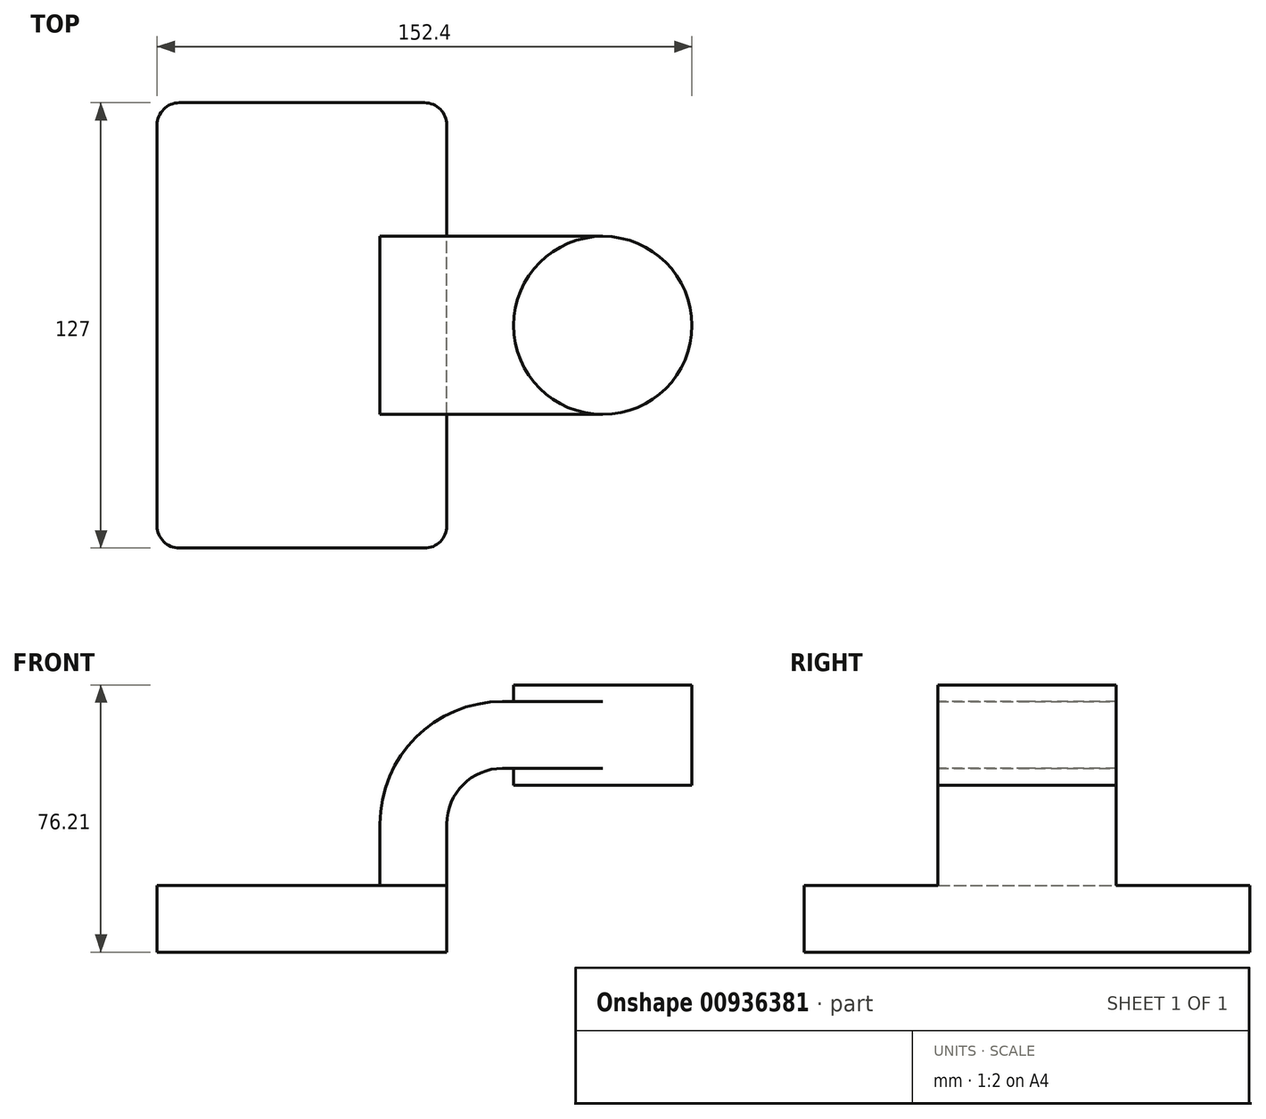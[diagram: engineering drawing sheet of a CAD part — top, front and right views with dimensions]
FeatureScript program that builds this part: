
annotation { "Feature Type Name" : "Feature", "Feature Type Description" : "" }
export const myFeature = defineFeature(function(context is Context, id is Id, definition is map)
    precondition{}
    {
        {
            var Q0;
            Q0=qCreatedBy(makeId("Front.planeOp"),FACE);
            var sketch = newSketch(context, id + "F0", { "sketchPlane" : qUnion([Q0])});
            skLineSegment(sketch, "E0.bottom", {"start": v(-41.28, 9.53) * mm, "end": v(41.28, 9.53) * mm});
            skLineSegment(sketch, "E0.top", {"start": v(-41.28, -9.52) * mm, "end": v(41.28, -9.52) * mm});
            skLineSegment(sketch, "E0.left", {"start": v(-41.28, 9.53) * mm, "end": v(-41.28, -9.52) * mm});
            skLineSegment(sketch, "E0.right", {"start": v(41.28, 9.53) * mm, "end": v(41.28, -9.52) * mm});
            skPoint(sketch, "E0.middle", {"position": v(0, 0) * mm});
            skLineSegment(sketch, "E1.bottom", {"start": v(60.33, 66.68) * mm, "end": v(111.12, 66.68) * mm});
            skLineSegment(sketch, "E1.top", {"start": v(60.33, 38.1) * mm, "end": v(111.12, 38.1) * mm});
            skLineSegment(sketch, "E1.left", {"start": v(60.33, 66.68) * mm, "end": v(60.32, 38.1) * mm});
            skLineSegment(sketch, "E1.right", {"start": v(111.12, 66.68) * mm, "end": v(111.12, 38.1) * mm});
            skPoint(sketch, "E1.middle", {"position": v(85.72, 52.39) * mm});
            skLineSegment(sketch, "E2", {"start": v(41.28, 9.53) * mm, "end": v(41.28, 27) * mm});
            skArc(sketch, "E3", {"start": v(41.28, 27) * mm, "mid": v(45.92, 38.23) * mm, "end": v(57.15, 42.88) * mm});
            skPoint(sketch, "E4.endSnap0", {"position": v(45.92, 38.23) * mm});
            skLineSegment(sketch, "E5", {"start": v(57.15, 42.88) * mm, "end": v(98.68, 42.88) * mm});
            skLineSegment(sketch, "E6.0", {"start": v(57.15, 61.93) * mm, "end": v(98.68, 61.93) * mm});
            skArc(sketch, "E6.1", {"start": v(22.23, 27) * mm, "mid": v(32.45, 51.7) * mm, "end": v(57.15, 61.93) * mm});
            skLineSegment(sketch, "E6.2", {"start": v(22.23, 9.53) * mm, "end": v(22.23, 27) * mm});
            skLineSegment(sketch, "E7", {"start": v(85.72, 38.1) * mm, "end": v(85.72, 66.68) * mm});
            skFitSpline(sketch, "E8", {"points": [v(-41.28, 9.53) * mm, v(57.15, 61.93) * mm], "startDerivative": vector(2.58, 99.04) * mm, "endDerivative": vector(241.72, -0.58) * mm});
            skSolve(sketch);
        }
        {
            var Q0;
            Q0=makeQuery(id+"F0.imprint","IMPRINT",FACE,{"disambiguationData":[TD([[makeQuery(id+"F0.imprint","IMPRINT",EDGE,{"derivedFrom":sQuery(id+"F0.wireOp",EDGE,"E0.top")}),1.0]])]});
            extrude(context, id + "F1", {"entities" : qUnion([Q0]), "depth" : 127 * mm, "offsetDistance" : 25.4 * mm, "symmetric" : true});
        }
        {
            var Q0;
            {var subQ1=sQuery(id+"F0.wireOp",EDGE,"E2");Q0=makeQuery(id+"F0.imprint","IMPRINT",FACE,{"disambiguationData":[TD([[makeQuery(id+"F0.imprint","IMPRINT",EDGE,{"derivedFrom":subQ1}),1.0]])]});}
            var Q1;
            {var subQ0=sQuery(id+"F0.wireOp",EDGE,"E6.0");var subQ1=sQuery(id+"F0.wireOp",EDGE,"E1.left");var subQ2=makeQuery(id+"F0.imprint","INTERSECT",VERTEX,{"derivedFrom":[subQ1,subQ0]});Q1=makeQuery(id+"F0.imprint","IMPRINT",FACE,{"disambiguationData":[TD([[makeQuery(id+"F0.imprint","IMPRINT",EDGE,{"disambiguationData":[TD([[subQ2,-1.0]])],"derivedFrom":subQ1}),1.0]])]});}
            extrude(context, id + "F2", {"entities" : qUnion([Q0, Q1]), "operationType" : NewBodyOperationType.ADD, "depth" : 50.8 * mm, "offsetDistance" : 25.4 * mm, "symmetric" : true});
        }
        {
            var Q0;
            Q0=makeQuery(id+"F0.imprint","IMPRINT",FACE,{"disambiguationData":[TD([[makeQuery(id+"F0.imprint","IMPRINT",EDGE,{"derivedFrom":sQuery(id+"F0.wireOp",EDGE,"E6.1")}),1.0]])]});
            extrude(context, id + "F3", {"entities" : qUnion([Q0]), "operationType" : NewBodyOperationType.ADD, "depth" : 15.88 * mm, "offsetDistance" : 25.4 * mm, "symmetric" : true});
        }
        {
            var Q0;
            {var subQ0=sQuery(id+"F0.wireOp",EDGE,"E1.right");Q0=makeQuery(id+"F0.imprint","IMPRINT",FACE,{"disambiguationData":[TD([[makeQuery(id+"F0.imprint","IMPRINT",EDGE,{"derivedFrom":subQ0}),-1.0]])]});}
            var Q1;
            Q1=sQuery(id+"F0.wireOp",EDGE,"E7");
            revolve(context, id + "F4", {"operationType" : NewBodyOperationType.ADD, "surfaceOperationType" : NewSurfaceOperationType.NEW, "entities" : qUnion([Q0]), "axis" : qUnion([Q1]), "revolveType" : RevolveType.FULL});
        }
        {
            var Q0;
            Q0=makeQuery(id+"F1.opExtrude","CAP_EDGE",EDGE,{"disambiguationData":[OSD([sQuery(id+"F0.wireOp",EDGE,"E0.left")])],"isStart":false});
            var Q1;
            Q1=makeQuery(id+"F1.opExtrude","CAP_EDGE",EDGE,{"disambiguationData":[OSD([sQuery(id+"F0.wireOp",EDGE,"E0.right")])],"isStart":false});
            var Q2;
            Q2=makeQuery(id+"F1.opExtrude","CAP_EDGE",EDGE,{"disambiguationData":[OSD([sQuery(id+"F0.wireOp",EDGE,"E0.left")])],"isStart":true});
            var Q3;
            Q3=makeQuery(id+"F1.opExtrude","CAP_EDGE",EDGE,{"disambiguationData":[OSD([sQuery(id+"F0.wireOp",EDGE,"E0.right")])],"isStart":true});
            fillet(context, id + "F5", {"entities" : qUnion([Q0, Q1, Q2, Q3]), "radius" : 6.35 * mm, "tangentPropagation" : true, "allowEdgeOverflow" : false});
        }
    });
